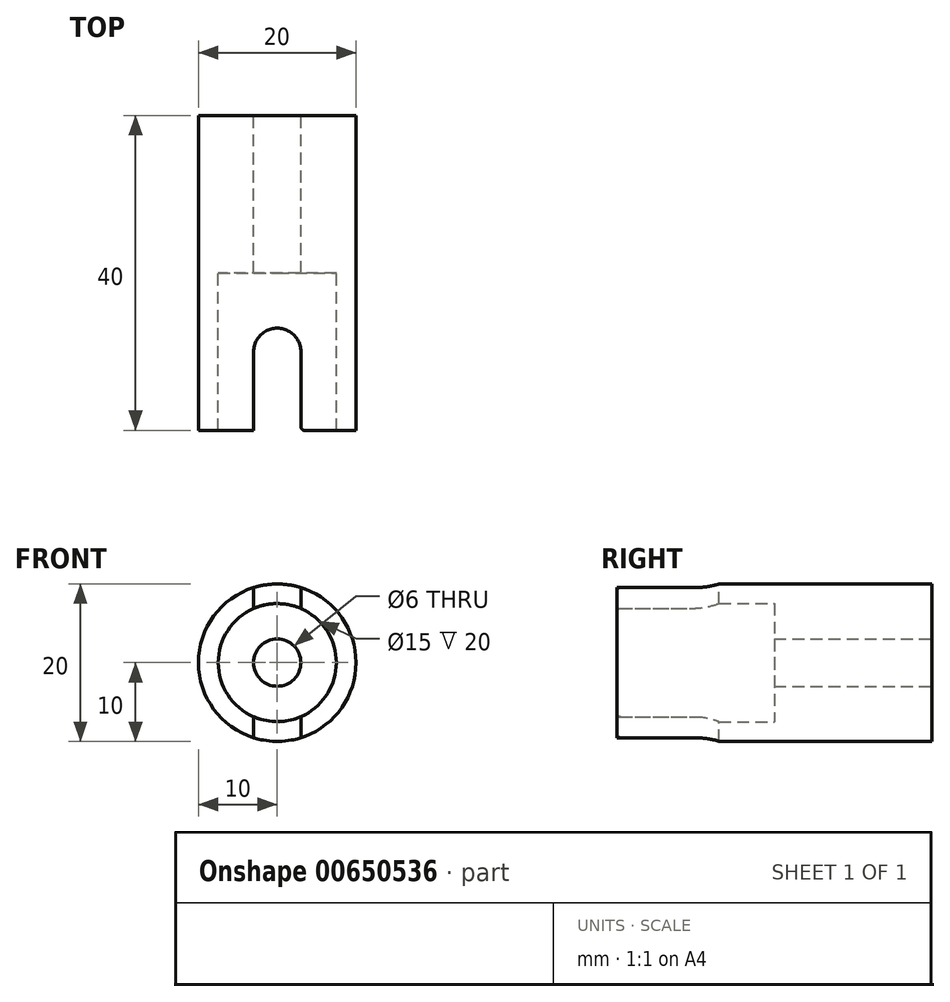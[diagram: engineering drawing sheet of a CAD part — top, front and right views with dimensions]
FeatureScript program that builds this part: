
annotation { "Feature Type Name" : "Feature", "Feature Type Description" : "" }
export const myFeature = defineFeature(function(context is Context, id is Id, definition is map)
    precondition{}
    {
        {
            var Q0;
            Q0=qCreatedBy(makeId("Right.planeOp"),FACE);
            var sketch = newSketch(context, id + "F0", { "sketchPlane" : qUnion([Q0])});
            skLineSegment(sketch, "E0", {"start": v(0, 3) * mm, "end": v(-20, 3) * mm});
            skLineSegment(sketch, "E1", {"start": v(-20, 3) * mm, "end": v(-20, 7.5) * mm});
            skLineSegment(sketch, "E2", {"start": v(-20, 7.5) * mm, "end": v(-40, 7.5) * mm});
            skLineSegment(sketch, "E3", {"start": v(-40, 7.5) * mm, "end": v(-40, 10) * mm});
            skLineSegment(sketch, "E4", {"start": v(-40, 10) * mm, "end": v(0, 10) * mm});
            skLineSegment(sketch, "E5", {"start": v(0, 10) * mm, "end": v(0, 3) * mm});
            skLineSegment(sketch, "E6", {"start": v(0, 0) * mm, "end": v(-21.31, 0) * mm, "construction": true});
            skSolve(sketch);
        }
        {
            var Q0;
            Q0=makeQuery(id+"F0.imprint","IMPRINT",FACE,{"disambiguationData":[TD([[makeQuery(id+"F0.imprint","IMPRINT",EDGE,{"derivedFrom":sQuery(id+"F0.wireOp",EDGE,"E0")}),-1.0]])]});
            var Q1;
            Q1=sQuery(id+"F0.wireOp",EDGE,"E6");
            revolve(context, id + "F1", {"entities" : qUnion([Q0]), "axis" : qUnion([Q1]), "revolveType" : RevolveType.FULL});
        }
        {
            var Q0;
            Q0=qCreatedBy(makeId("Top.planeOp"),FACE);
            var sketch = newSketch(context, id + "F2", { "sketchPlane" : qUnion([Q0])});
            skLineSegment(sketch, "E7", {"start": v(-3, -40) * mm, "end": v(-3, -30) * mm});
            skLineSegment(sketch, "E8", {"start": v(3, -40) * mm, "end": v(3, -30) * mm});
            skArc(sketch, "E9", {"start": v(3, -30) * mm, "mid": v(0, -27) * mm, "end": v(-3, -30) * mm});
            skLineSegment(sketch, "E10", {"start": v(-3, -40) * mm, "end": v(3, -40) * mm});
            skSolve(sketch);
        }
        {
            var Q0;
            Q0=makeQuery(id+"F2.imprint","IMPRINT",FACE,{"disambiguationData":[TD([[makeQuery(id+"F2.imprint","IMPRINT",EDGE,{"derivedFrom":sQuery(id+"F2.wireOp",EDGE,"E7")}),-1.0]])]});
            extrude(context, id + "F3", {"entities" : qUnion([Q0]), "operationType" : NewBodyOperationType.REMOVE, "endBound" : BoundingType.THROUGH_ALL, "oppositeDirection" : true, "depth" : 25 * mm, "offsetDistance" : 25 * mm, "hasSecondDirection" : true, "secondDirectionBound" : SecondDirectionBoundingType.THROUGH_ALL, "secondDirectionOppositeDirection" : false, "secondDirectionDepth" : 25 * mm});
        }
        {
            var Q0;
            Q0=makeQuery(id+"F3.boolean.opBoolean","COPY",EDGE,{"disambiguationData":[OD(1.0)],"derivedFrom":makeQuery(id+"F3.opExtrude","SWEPT_EDGE",EDGE,{"disambiguationData":[OSD([sQuery(id+"F2.wireOp",EDGE,"E7"),sQuery(id+"F2.wireOp",EDGE,"E10")])]})});
            var Q1;
            Q1=makeQuery(id+"F3.boolean.opBoolean","COPY",EDGE,{"disambiguationData":[OD(1.0)],"derivedFrom":makeQuery(id+"F3.opExtrude","SWEPT_EDGE",EDGE,{"disambiguationData":[OSD([sQuery(id+"F2.wireOp",EDGE,"E8"),sQuery(id+"F2.wireOp",EDGE,"E10")])]})});
            var Q2;
            Q2=makeQuery(id+"F3.boolean.opBoolean","COPY",EDGE,{"disambiguationData":[OD(0.0)],"derivedFrom":makeQuery(id+"F3.opExtrude","SWEPT_EDGE",EDGE,{"disambiguationData":[OSD([sQuery(id+"F2.wireOp",EDGE,"E8"),sQuery(id+"F2.wireOp",EDGE,"E10")])]})});
            var Q3;
            Q3=makeQuery(id+"F3.boolean.opBoolean","COPY",EDGE,{"disambiguationData":[OD(0.0)],"derivedFrom":makeQuery(id+"F3.opExtrude","SWEPT_EDGE",EDGE,{"disambiguationData":[OSD([sQuery(id+"F2.wireOp",EDGE,"E7"),sQuery(id+"F2.wireOp",EDGE,"E10")])]})});
            fillet(context, id + "F4", {"entities" : qUnion([Q0, Q1, Q2, Q3]), "radius" : .5 * mm, "tangentPropagation" : true, "allowEdgeOverflow" : false});
        }
    });
